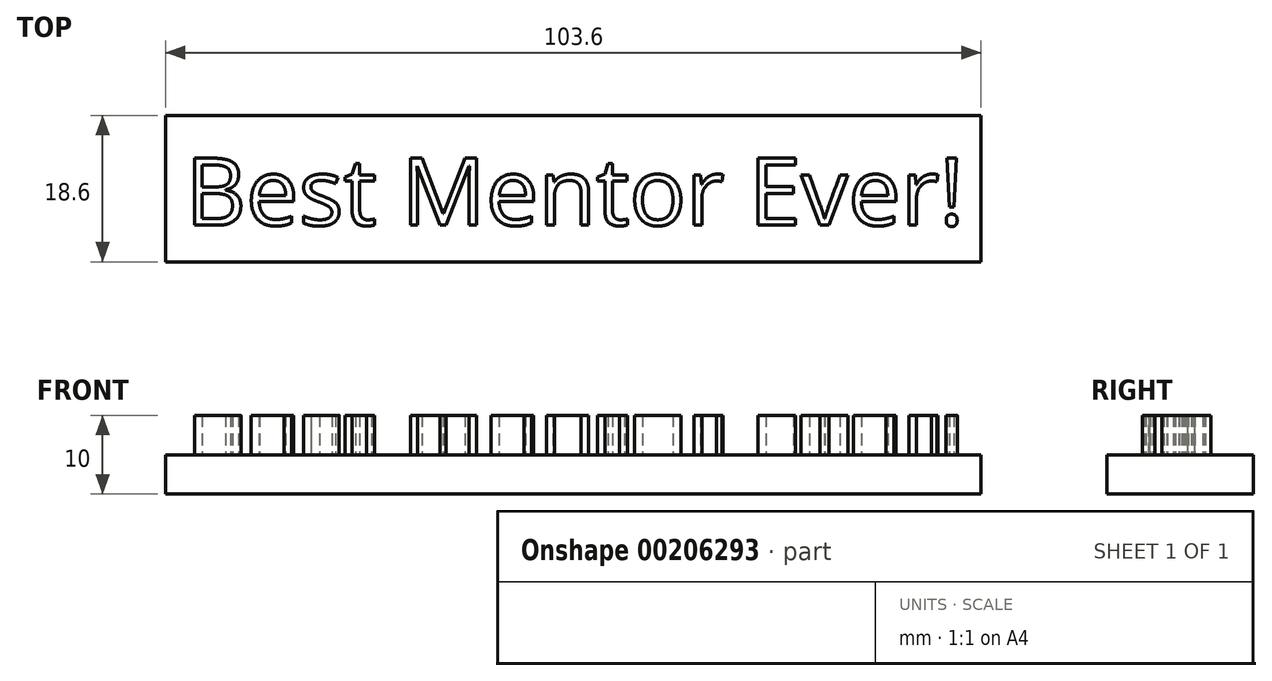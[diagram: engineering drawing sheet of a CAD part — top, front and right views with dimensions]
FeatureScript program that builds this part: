
annotation { "Feature Type Name" : "Feature", "Feature Type Description" : "" }
export const myFeature = defineFeature(function(context is Context, id is Id, definition is map)
    precondition{}
    {
        {
            var Q0;
            Q0=qCreatedBy(makeId("Top.planeOp"),FACE);
            var sketch = newSketch(context, id + "F0", { "sketchPlane" : qUnion([Q0])});
            skLineSegment(sketch, "E0.bottom", {"start": v(-39.23, 13.95) * mm, "end": v(64.37, 13.95) * mm});
            skLineSegment(sketch, "E0.top", {"start": v(-39.23, -4.65) * mm, "end": v(64.37, -4.65) * mm});
            skLineSegment(sketch, "E0.left", {"start": v(-39.23, 13.95) * mm, "end": v(-39.23, -4.65) * mm});
            skLineSegment(sketch, "E0.right", {"start": v(64.37, 13.95) * mm, "end": v(64.37, -4.65) * mm});
            skSolve(sketch);
        }
        {
            var Q0;
            Q0 = qSketchRegion(id + "F0", true);
            extrude(context, id + "F1", {"entities" : qUnion([Q0]), "depth" : 5 * mm});
        }
        {
            var Q0;
            Q0=makeQuery(id+"F1.opExtrude","CAP_FACE",FACE,{"disambiguationData":[OSD([sQuery(id+"F0.wireOp",EDGE,"E0.bottom"),sQuery(id+"F0.wireOp",EDGE,"E0.top"),sQuery(id+"F0.wireOp",EDGE,"E0.left"),sQuery(id+"F0.wireOp",EDGE,"E0.right")])],"isStart":false});
            var sketch = newSketch(context, id + "F2", { "sketchPlane" : qUnion([Q0])});
            skText(sketch, "E1", { "text": "Best Mentor Ever!", "fontName": "OpenSans-Regular.ttf"});
            const initialGuessF2  = {"E1": [-0.03673, 0, 1, 0, 0.00859]};
            skSetInitialGuess(sketch, initialGuessF2);
            skSolve(sketch);
        }
        {
            var Q0;
            Q0 = qSketchRegion(id + "F2", true);
            extrude(context, id + "F3", {"entities" : qUnion([Q0]), "operationType" : NewBodyOperationType.ADD, "depth" : 5 * mm});
        }
    });
